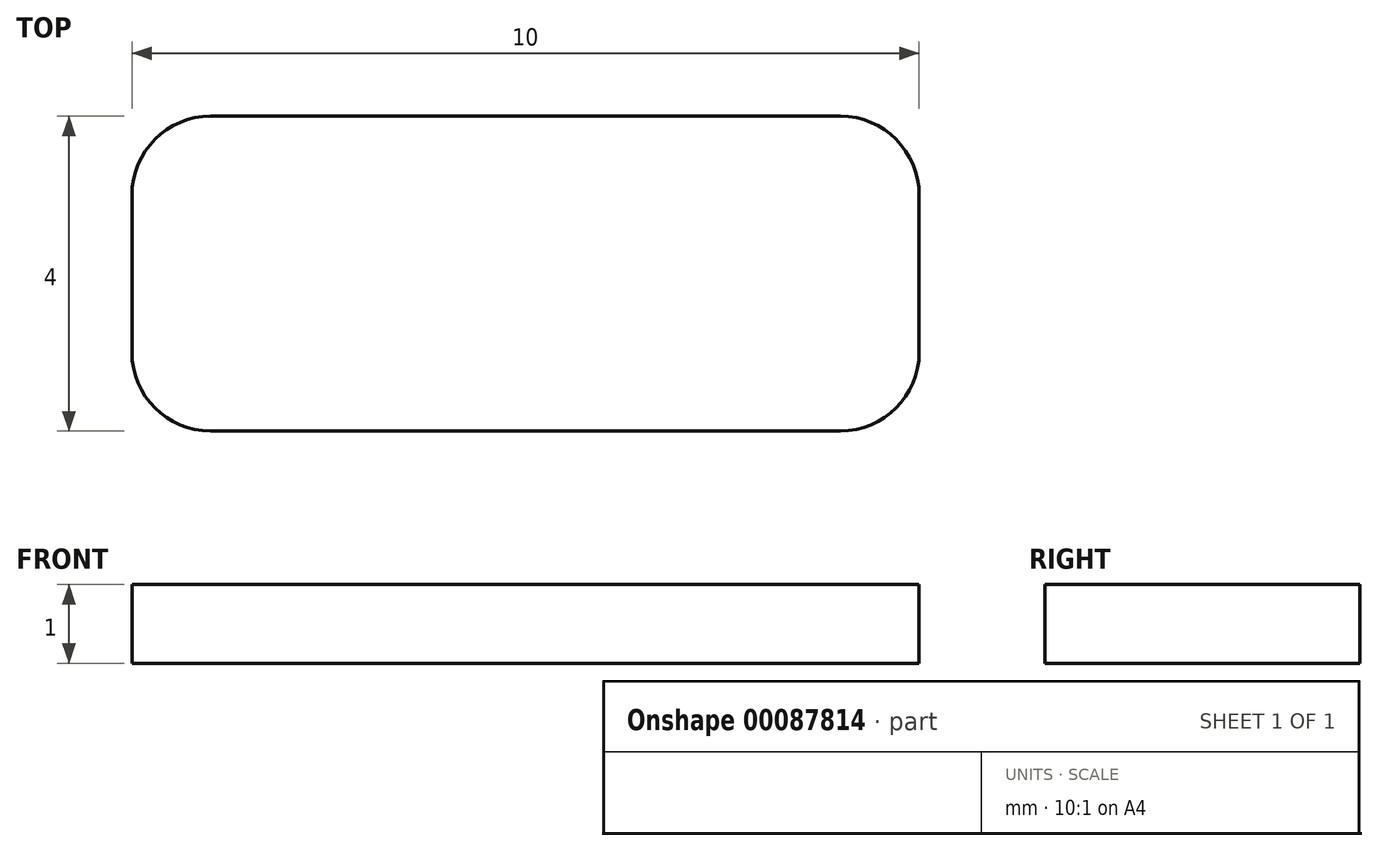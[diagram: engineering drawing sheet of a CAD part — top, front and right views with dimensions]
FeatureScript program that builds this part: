
annotation { "Feature Type Name" : "Feature", "Feature Type Description" : "" }
export const myFeature = defineFeature(function(context is Context, id is Id, definition is map)
    precondition{}
    {
        {
            var Q0;
            Q0=qCreatedBy(makeId("Top.planeOp"),FACE);
            var sketch = newSketch(context, id + "F0", { "sketchPlane" : qUnion([Q0])});
            skLineSegment(sketch, "E0.bottom", {"start": v(5, -2) * mm, "end": v(-5, -2) * mm});
            skLineSegment(sketch, "E0.top", {"start": v(5, 2) * mm, "end": v(-5, 2) * mm});
            skLineSegment(sketch, "E0.left", {"start": v(5, -2) * mm, "end": v(5, 2) * mm});
            skLineSegment(sketch, "E0.right", {"start": v(-5, -2) * mm, "end": v(-5, 2) * mm});
            skPoint(sketch, "E0.middle", {"position": v(0, 0) * mm});
            skSolve(sketch);
        }
        {
            var Q0;
            Q0=qSketchRegion(id+"F0",true);
            extrude(context, id + "F1", {"entities" : qUnion([Q0]), "depth" : 1 * mm});
        }
        {
            var Q0;
            Q0=makeQuery(id+"F1.opExtrude","SWEPT_EDGE",EDGE,{"disambiguationData":[OSD([sQuery(id+"F0.wireOp",EDGE,"E0.bottom"),sQuery(id+"F0.wireOp",EDGE,"E0.left")])]});
            var Q1;
            Q1=makeQuery(id+"F1.opExtrude","SWEPT_EDGE",EDGE,{"disambiguationData":[OSD([sQuery(id+"F0.wireOp",EDGE,"E0.top"),sQuery(id+"F0.wireOp",EDGE,"E0.left")])]});
            var Q2;
            Q2=makeQuery(id+"F1.opExtrude","SWEPT_EDGE",EDGE,{"disambiguationData":[OSD([sQuery(id+"F0.wireOp",EDGE,"E0.top"),sQuery(id+"F0.wireOp",EDGE,"E0.right")])]});
            var Q3;
            Q3=makeQuery(id+"F1.opExtrude","SWEPT_EDGE",EDGE,{"disambiguationData":[OSD([sQuery(id+"F0.wireOp",EDGE,"E0.bottom"),sQuery(id+"F0.wireOp",EDGE,"E0.right")])]});
            fillet(context, id + "F2", {"entities" : qUnion([Q0, Q1, Q2, Q3]), "radius" : 1 * mm, "tangentPropagation" : true, "allowEdgeOverflow" : false});
        }
    });
